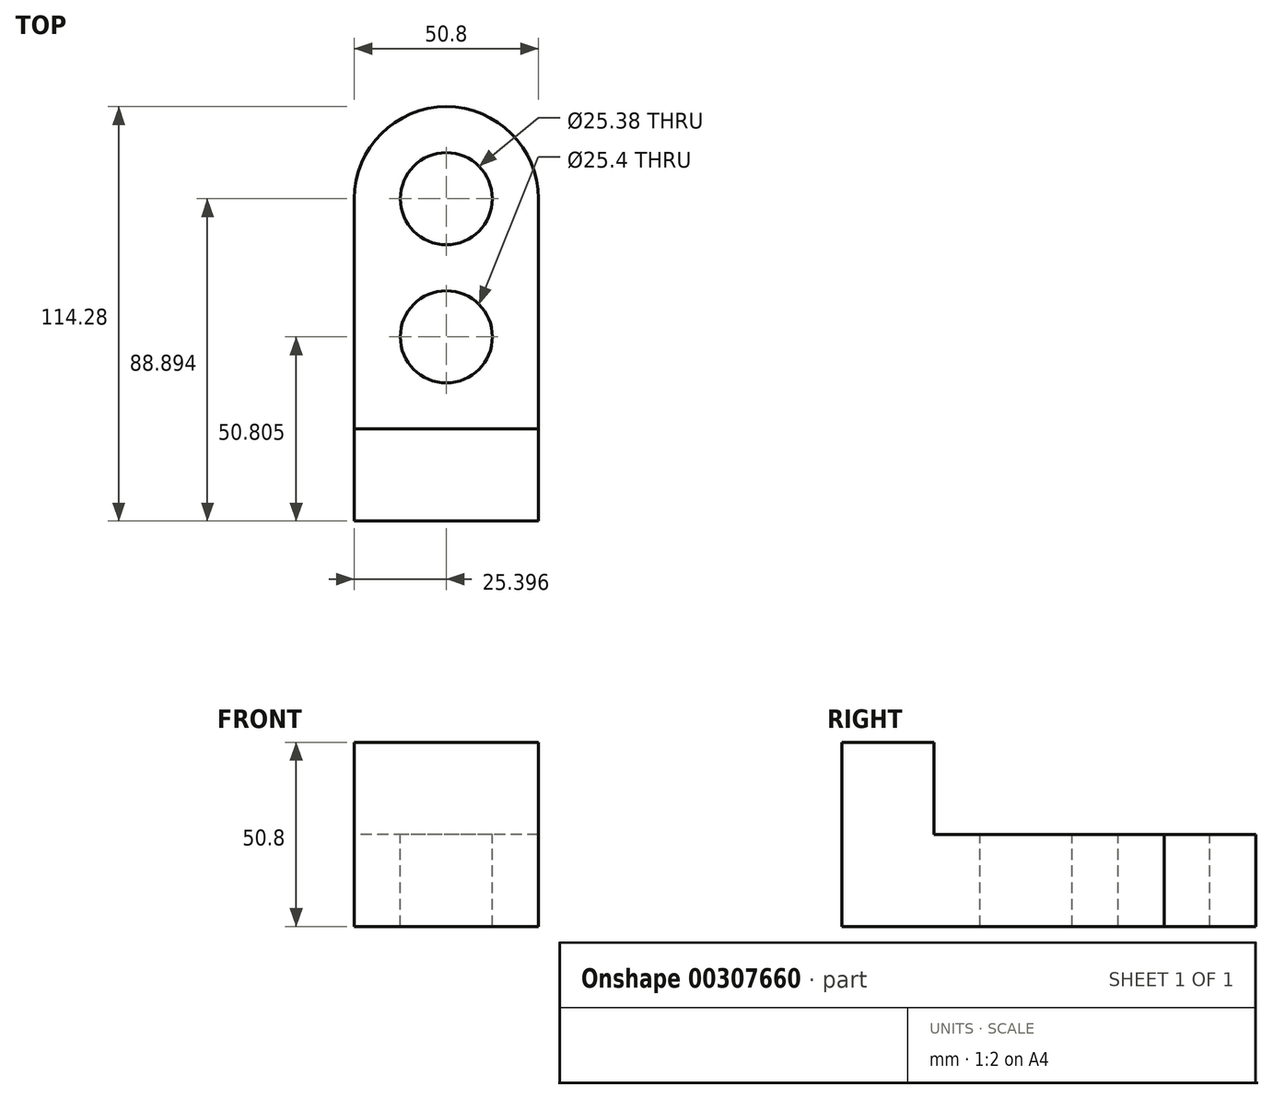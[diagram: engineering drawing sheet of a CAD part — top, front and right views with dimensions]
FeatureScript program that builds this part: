
annotation { "Feature Type Name" : "Feature", "Feature Type Description" : "" }
export const myFeature = defineFeature(function(context is Context, id is Id, definition is map)
    precondition{}
    {
        {
            var Q0;
            Q0=qCreatedBy(makeId("Top.planeOp"),FACE);
            var sketch = newSketch(context, id + "F0", { "sketchPlane" : qUnion([Q0])});
            skLineSegment(sketch, "E0.bottom", {"start": v(-60.42, 55.21) * mm, "end": v(-60.4, 55.21) * mm});
            skLineSegment(sketch, "E0.top", {"start": v(-60.42, -33.69) * mm, "end": v(-9.62, -33.69) * mm});
            skLineSegment(sketch, "E0.left", {"start": v(-60.42, 55.21) * mm, "end": v(-60.42, -33.69) * mm});
            skLineSegment(sketch, "E0.right", {"start": v(-9.62, 55.21) * mm, "end": v(-9.62, -33.69) * mm});
            skPoint(sketch, "E1.startSnap0", {"position": v(-35.02, 55.21) * mm});
            skArc(sketch, "E2", {"start": v(-9.65, 55.21) * mm, "mid": v(-35.02, 80.6) * mm, "end": v(-60.4, 55.21) * mm});
            skLineSegment(sketch, "E3.trimOffspring", {"start": v(-9.65, 55.21) * mm, "end": v(-9.62, 55.21) * mm});
            skSolve(sketch);
        }
        {
            var Q0;
            Q0=makeQuery(id+"F0.imprint","IMPRINT",FACE,{"disambiguationData":[TD([[makeQuery(id+"F0.imprint","IMPRINT",EDGE,{"derivedFrom":sQuery(id+"F0.wireOp",EDGE,"E0.bottom")}),-1.0]])]});
            var Q1;
            Q1=makeQuery(id+"F0.imprint","IMPRINT",FACE,{"disambiguationData":[TD([[makeQuery(id+"F0.imprint","IMPRINT",EDGE,{"derivedFrom":sQuery(id+"F0.wireOp",EDGE,"E0.bottom")}),1.0]])]});
            extrude(context, id + "F1", {"entities" : qUnion([Q0, Q1]), "depth" : 25.4 * mm});
        }
        {
            var Q0;
            Q0=makeQuery(id+"F1.opExtrude","CAP_FACE",FACE,{"disambiguationData":[OSD([sQuery(id+"F0.wireOp",EDGE,"E0.bottom"),sQuery(id+"F0.wireOp",EDGE,"E0.top"),sQuery(id+"F0.wireOp",EDGE,"E0.left"),sQuery(id+"F0.wireOp",EDGE,"E0.right"),sQuery(id+"F0.wireOp",EDGE,"E2"),sQuery(id+"F0.wireOp",EDGE,"E3.trimOffspring")])],"isStart":false});
            var sketch = newSketch(context, id + "F2", { "sketchPlane" : qUnion([Q0])});
            skLineSegment(sketch, "E4", {"start": v(-60.42, -33.69) * mm, "end": v(-9.62, -33.69) * mm});
            skLineSegment(sketch, "E5", {"start": v(-9.62, -33.69) * mm, "end": v(-9.62, -8.29) * mm});
            skLineSegment(sketch, "E6", {"start": v(-9.62, -8.29) * mm, "end": v(-60.42, -8.29) * mm});
            skLineSegment(sketch, "E7", {"start": v(-60.42, -8.29) * mm, "end": v(-60.42, -33.69) * mm});
            skSolve(sketch);
        }
        {
            var Q0;
            Q0 = qSketchRegion(id + "F2", true);
            extrude(context, id + "F3", {"entities" : qUnion([Q0]), "operationType" : NewBodyOperationType.ADD, "depth" : 25.4 * mm});
        }
        {
            var Q0;
            Q0=makeQuery(id+"F1.opExtrude","CAP_FACE",FACE,{"disambiguationData":[OSD([sQuery(id+"F0.wireOp",EDGE,"E0.bottom"),sQuery(id+"F0.wireOp",EDGE,"E0.top"),sQuery(id+"F0.wireOp",EDGE,"E0.left"),sQuery(id+"F0.wireOp",EDGE,"E0.right"),sQuery(id+"F0.wireOp",EDGE,"E2"),sQuery(id+"F0.wireOp",EDGE,"E3.trimOffspring")])],"isStart":false});
            var sketch = newSketch(context, id + "F4", { "sketchPlane" : qUnion([Q0])});
            skCircle(sketch, "E8", {"center": v(-35.02, 17.11) * mm, "radius": 12.7 * mm});
            skPoint(sketch, "E8.centerSnap0", {"position": v(-35.02, -8.29) * mm});
            skCircle(sketch, "E9", {"center": v(-35.02, 55.2) * mm, "radius": 12.69 * mm});
            skLineSegment(sketch, "E10", {"start": v(-35.02, 29.81) * mm, "end": v(-35.02, 4.41) * mm});
            skLineSegment(sketch, "E11", {"start": v(-35.02, 42.51) * mm, "end": v(-35.02, 67.9) * mm});
            skLineSegment(sketch, "E12", {"start": v(-35.02, 55.2) * mm, "end": v(-22.34, 55.2) * mm});
            skLineSegment(sketch, "E13", {"start": v(-35.02, 55.2) * mm, "end": v(-47.71, 55.2) * mm});
            skLineSegment(sketch, "E14", {"start": v(-35.02, 17.11) * mm, "end": v(-22.32, 17.11) * mm});
            skLineSegment(sketch, "E15", {"start": v(-35.02, 17.11) * mm, "end": v(-47.72, 17.11) * mm});
            skSolve(sketch);
        }
        {
            var Q0;
            Q0 = qSketchRegion(id + "F4", true);
            extrude(context, id + "F5", {"entities" : qUnion([Q0]), "operationType" : NewBodyOperationType.REMOVE, "oppositeDirection" : true, "depth" : 25.4 * mm});
        }
    });
